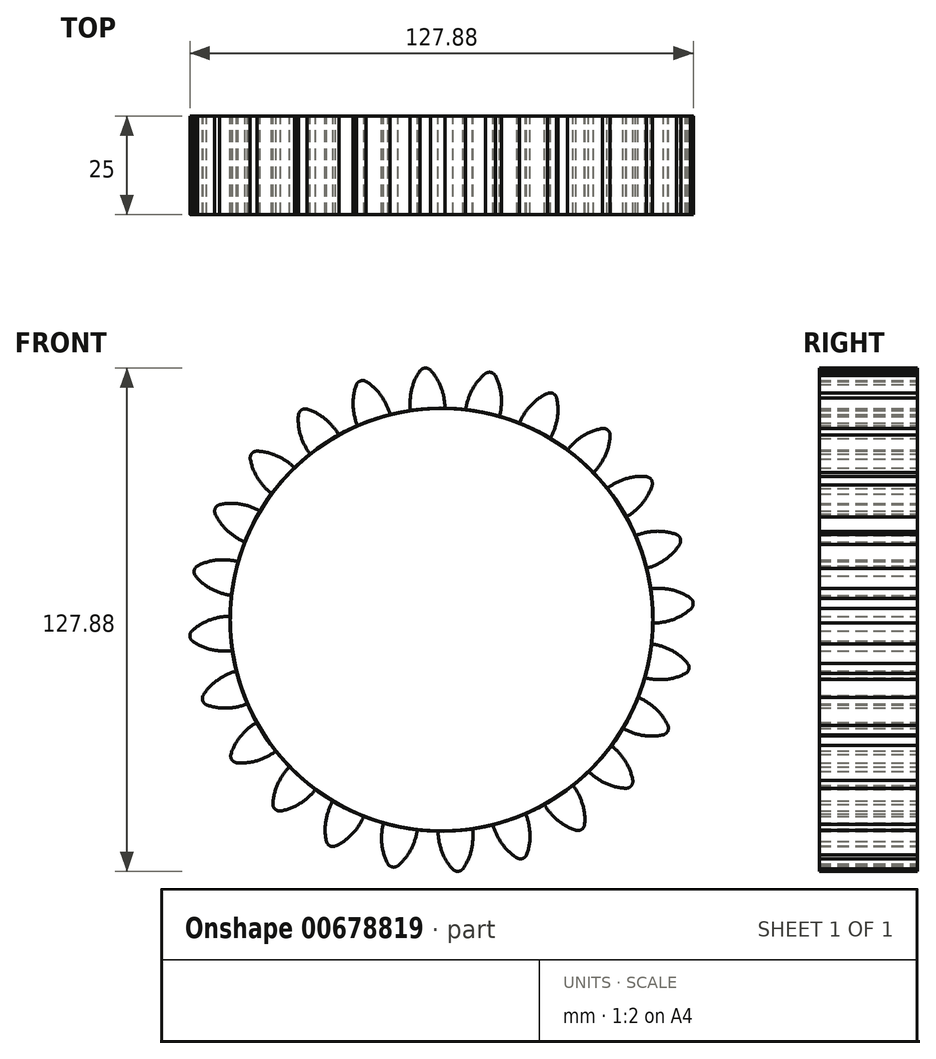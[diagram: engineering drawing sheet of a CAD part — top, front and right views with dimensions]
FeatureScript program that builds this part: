
annotation { "Feature Type Name" : "Feature", "Feature Type Description" : "" }
export const myFeature = defineFeature(function(context is Context, id is Id, definition is map)
    precondition{}
    {
        {
            var Q0;
            Q0=qCreatedBy(makeId("Front.planeOp"),FACE);
            var sketch = newSketch(context, id + "F0", { "sketchPlane" : qUnion([Q0])});
            skCircle(sketch, "E0", {"center": v(0, 0) * mm, "radius": 53.72 * mm});
            skCircle(sketch, "E1", {"center": v(0, 0) * mm, "radius": 58.67 * mm, "construction": true});
            skCircle(sketch, "E2", {"center": v(0, 0) * mm, "radius": 63.5 * mm, "construction": true});
            skLineSegment(sketch, "E3", {"start": v(0, 0) * mm, "end": v(0, 90.28) * mm, "construction": true});
            skLineSegment(sketch, "E4", {"start": v(0, 0) * mm, "end": v(-5.89, 89.83) * mm, "construction": true});
            skLineSegment(sketch, "E5", {"start": v(0, 58.67) * mm, "end": v(-86.47, 27.2) * mm, "construction": true});
            skLineSegment(sketch, "E6", {"start": v(0, 58.67) * mm, "end": v(-89.07, 58.67) * mm, "construction": true});
            skCircle(sketch, "E7", {"center": v(0, 0) * mm, "radius": 55.14 * mm, "construction": true});
            skCircle(sketch, "E8", {"center": v(0, 58.67) * mm, "radius": 14.6 * mm, "construction": true});
            skCircle(sketch, "E9", {"center": v(-13.72, 53.68) * mm, "radius": 14.6 * mm, "construction": true});
            skArc(sketch, "E10", {"start": v(0, 58.67) * mm, "mid": v(-1.18, 61.2) * mm, "end": v(-2.86, 63.44) * mm});
            skArc(sketch, "E11", {"start": v(0.88, 53.71) * mm, "mid": v(0.64, 56.23) * mm, "end": v(0, 58.67) * mm});
            skArc(sketch, "E12.MirrorCS", {"start": v(-7.88, 53.14) * mm, "mid": v(-7.97, 55.66) * mm, "end": v(-7.66, 58.17) * mm});
            skArc(sketch, "E13.MirrorCS", {"start": v(-7.66, 58.17) * mm, "mid": v(-6.82, 60.83) * mm, "end": v(-5.45, 63.27) * mm});
            skArc(sketch, "E14", {"start": v(-2.86, 63.44) * mm, "mid": v(-4.2, 63.93) * mm, "end": v(-5.45, 63.27) * mm});
            skSolve(sketch);
        }
        {
            var Q0;
            {var subQ0=sQuery(id+"F0.wireOp",EDGE,"E0");var subQ1=makeQuery(id+"F0.imprint","INTERSECT",VERTEX,{"derivedFrom":[subQ0,sQuery(id+"F0.wireOp",EDGE,"E12.MirrorCS")]});Q0=makeQuery(id+"F0.imprint","IMPRINT",FACE,{"disambiguationData":[TD([[makeQuery(id+"F0.imprint","IMPRINT",EDGE,{"disambiguationData":[TD([[subQ1,1.0]])],"derivedFrom":subQ0}),1.0]])]});}
            var Q1;
            Q1=makeQuery(id+"F0.imprint","IMPRINT",FACE,{"disambiguationData":[TD([[makeQuery(id+"F0.imprint","IMPRINT",EDGE,{"derivedFrom":sQuery(id+"F0.wireOp",EDGE,"E10")}),1.0]])]});
            extrude(context, id + "F1", {"entities" : qUnion([Q0, Q1]), "depth" : 25 * mm, "offsetDistance" : 25 * mm});
        }
        {
            var Q0;
            Q0=makeQuery(id+"F1.opExtrude","SWEPT_BODY",BODY,{"disambiguationData":[OSD([sQuery(id+"F0.wireOp",EDGE,"E0"),sQuery(id+"F0.wireOp",EDGE,"E10"),sQuery(id+"F0.wireOp",EDGE,"E12.MirrorCS"),sQuery(id+"F0.wireOp",EDGE,"E13.MirrorCS"),sQuery(id+"F0.wireOp",EDGE,"E11"),sQuery(id+"F0.wireOp",EDGE,"E14")])]});
            var Q1;
            Q1=makeQuery(id+"F1.opExtrude","SWEPT_FACE",FACE,{"disambiguationData":[OSD([sQuery(id+"F0.wireOp",EDGE,"E0")])]});
            circularPattern(context, id + "F2", {"entities" : qUnion([Q0]), "axis" : qUnion([Q1]), "angle" : 360 * degree, "instanceCount" : 24, "equalSpace" : true});
        }
    });
